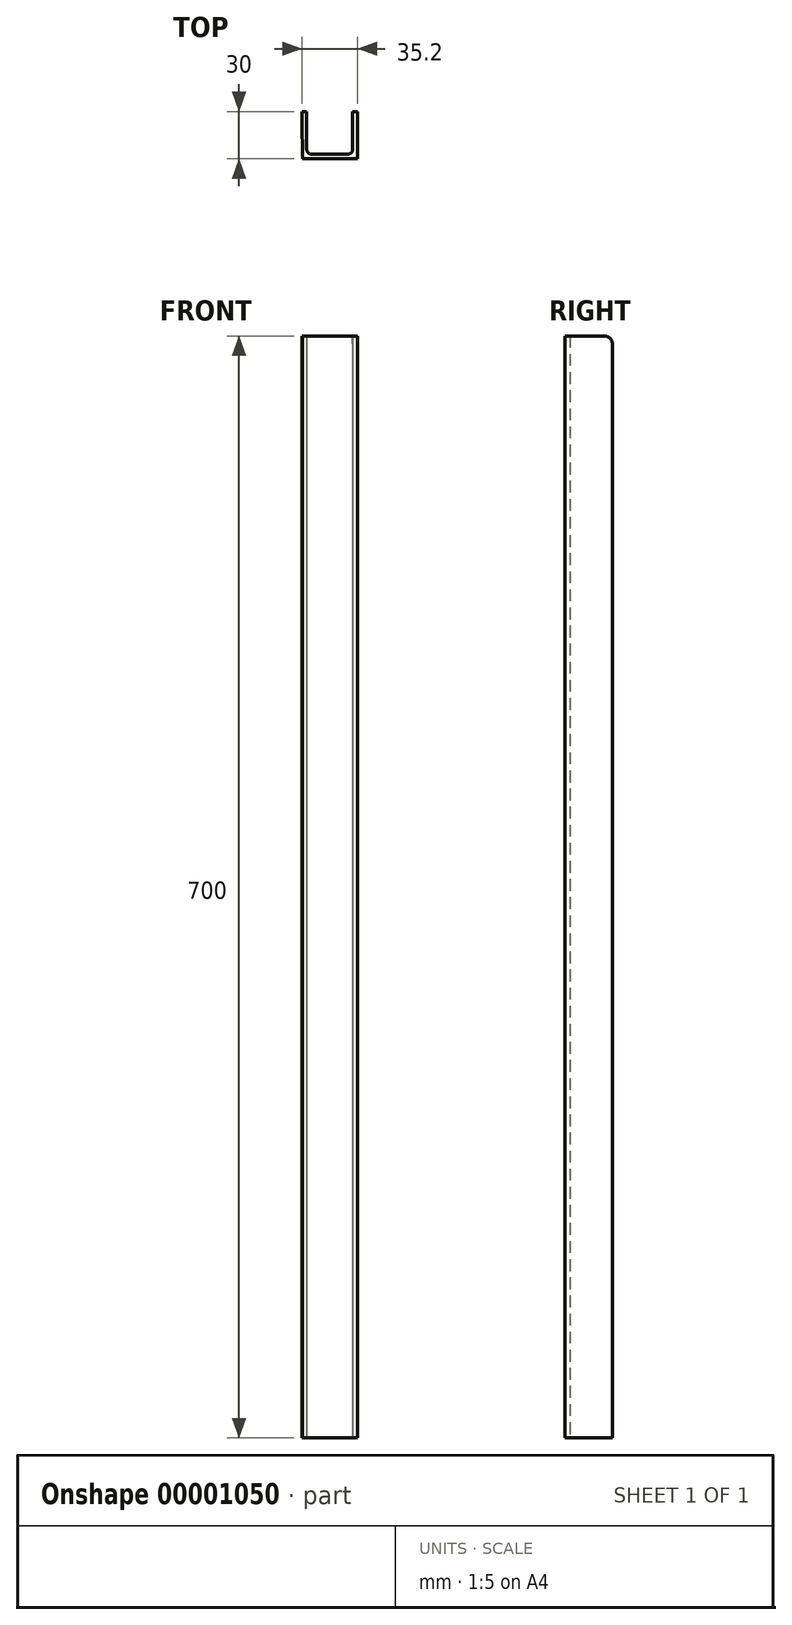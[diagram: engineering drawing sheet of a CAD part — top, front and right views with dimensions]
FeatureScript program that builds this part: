
annotation { "Feature Type Name" : "Feature", "Feature Type Description" : "" }
export const myFeature = defineFeature(function(context is Context, id is Id, definition is map)
    precondition{}
    {
        {
            var Q0;
            Q0=qCreatedBy(makeId("Top.planeOp"),FACE);
            var sketch = newSketch(context, id + "F0", { "sketchPlane" : qUnion([Q0])});
            skLineSegment(sketch, "E0", {"start": v(-17.42, -8.6) * mm, "end": v(17.58, -8.6) * mm});
            skLineSegment(sketch, "E1", {"start": v(17.58, -8.6) * mm, "end": v(17.58, 21.4) * mm});
            skLineSegment(sketch, "E2", {"start": v(17.58, 21.4) * mm, "end": v(14.58, 21.4) * mm});
            skLineSegment(sketch, "E3", {"start": v(14.58, 21.4) * mm, "end": v(14.58, -2.6) * mm});
            skLineSegment(sketch, "E4", {"start": v(11.58, -5.6) * mm, "end": v(-11.62, -5.6) * mm});
            skLineSegment(sketch, "E5", {"start": v(-14.62, -2.6) * mm, "end": v(-14.62, 21.4) * mm});
            skLineSegment(sketch, "E6", {"start": v(-14.62, 21.4) * mm, "end": v(-17.62, 21.4) * mm});
            skLineSegment(sketch, "E7", {"start": v(-17.62, 21.4) * mm, "end": v(-17.42, -8.6) * mm});
            skPoint(sketch, "E8.visualSharp", {"position": v(-14.62, -5.6) * mm});
            skArc(sketch, "E8.filletArc", {"start": v(-14.62, -2.6) * mm, "mid": v(-13.74, -4.72) * mm, "end": v(-11.62, -5.6) * mm});
            skPoint(sketch, "E9.visualSharp", {"position": v(14.58, -5.6) * mm});
            skArc(sketch, "E9.filletArc", {"start": v(11.58, -5.6) * mm, "mid": v(13.7, -4.72) * mm, "end": v(14.58, -2.6) * mm});
            skSolve(sketch);
        }
        {
            var Q0;
            Q0=makeQuery(id+"F0.imprint","IMPRINT",FACE,{"disambiguationData":[TD([[makeQuery(id+"F0.imprint","IMPRINT",EDGE,{"derivedFrom":sQuery(id+"F0.wireOp",EDGE,"E0")}),1.0]])]});
            extrude(context, id + "F1", {"entities" : qUnion([Q0]), "depth" : 700 * mm, "offsetDistance" : 25 * mm});
        }
        {
            var Q0;
            Q0=makeQuery(id+"F1.opExtrude","CAP_EDGE",EDGE,{"disambiguationData":[OSD([sQuery(id+"F0.wireOp",EDGE,"E2")])],"isStart":false});
            var Q1;
            Q1=makeQuery(id+"F1.opExtrude","CAP_EDGE",EDGE,{"disambiguationData":[OSD([sQuery(id+"F0.wireOp",EDGE,"E6")])],"isStart":false});
            fillet(context, id + "F2", {"entities" : qUnion([Q0, Q1]), "radius" : 5 * mm, "tangentPropagation" : true, "allowEdgeOverflow" : false});
        }
    });
